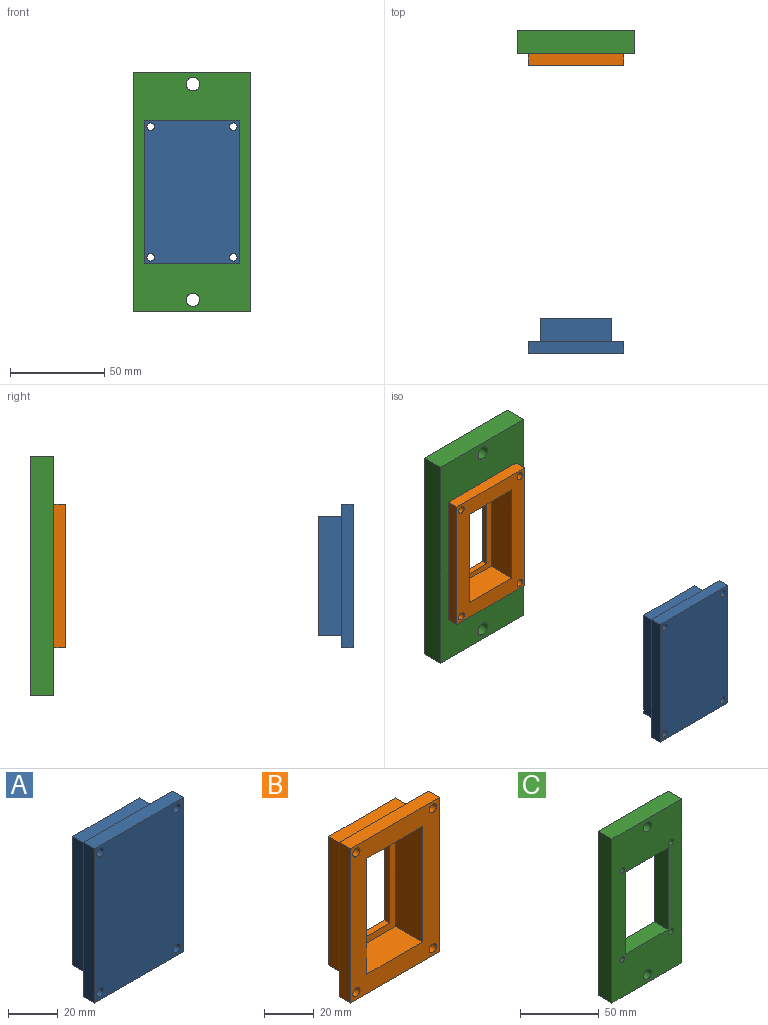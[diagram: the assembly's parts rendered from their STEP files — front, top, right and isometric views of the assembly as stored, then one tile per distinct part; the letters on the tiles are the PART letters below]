
ASSEMBLY  parts=3 mates=4
PART A: 15 faces, bbox 50.8x18.5x76.2 mm
  f0: plane 63.5x12.19mm, normal (1,0,0), area 774.2mm2, adj f1,f3,f4,f10
  f1: plane 38.1x12.19mm, normal (0,0,1), area 464.5mm2, adj f0,f2,f4,f10
  f2: plane 63.5x12.19mm, normal (-1,0,0), area 774.2mm2, adj f1,f3,f4,f10
  f3: plane 38.1x12.19mm, normal (0,0,-1), area 464.5mm2, adj f0,f2,f4,f10
  f4: plane 63.5x38.1mm, normal (0,1,0), area 2419.3mm2, adj f0,f1,f2,f3
  f5: plane 76.2x6.35mm, normal (1,0,0), area 483.9mm2, adj f6,f8,f9,f10
  f6: plane 50.8x6.35mm, normal (0,0,1), area 322.6mm2, adj f5,f7,f9,f10
  f7: plane 76.2x6.35mm, normal (-1,0,0), area 483.9mm2, adj f6,f8,f9,f10
  f8: plane 50.8x6.35mm, normal (0,0,-1), area 322.6mm2, adj f5,f7,f9,f10
  f9: plane 76.2x50.8mm, normal (0,-1,0), area 3817.4mm2, adj f5,f6,f7,f8,f11,f12,f13,f14
  f10: plane 76.2x50.8mm, normal (0,1,0), area 1398.1mm2, adj f0,f1,f2,f3,f5,f6,f7,f8
  f11: cylinder r=2.06mm len=6.35mm, axis (0,1,0), area 82.3mm2, adj f9,f10
  f12: cylinder r=2.06mm len=6.35mm, axis (0,1,0), area 82.3mm2, adj f9,f10
  f13: cylinder r=2.06mm len=6.35mm, axis (0,1,0), area 82.3mm2, adj f9,f10
  f14: cylinder r=2.06mm len=6.35mm, axis (0,1,0), area 82.3mm2, adj f9,f10
PART B: 24 faces, bbox 50.8x18.5x76.2 mm
  f0: plane 76.2x50.8mm, normal (0,-1,0), area 2002.9mm2, adj f10,f11,f12,f13,f15,f16,f17,f18
  f1: plane 50.8x3.05mm, normal (-1,0,0), area 154.8mm2, adj f2,f4,f5,f23
  f2: plane 25.4x3.05mm, normal (0,0,-1), area 77.4mm2, adj f1,f3,f5,f23
  f3: plane 50.8x3.05mm, normal (1,0,0), area 154.8mm2, adj f2,f4,f5,f23
  f4: plane 25.4x3.05mm, normal (0,0,1), area 77.4mm2, adj f1,f3,f5,f23
  f5: plane 63.5x38.1mm, normal (0,1,0), area 1129mm2, adj f1,f2,f3,f4,f6,f7,f8,f9
  f6: plane 63.5x12.19mm, normal (1,0,0), area 774.2mm2, adj f5,f7,f9,f14
  f7: plane 38.1x12.19mm, normal (0,0,1), area 464.5mm2, adj f5,f6,f8,f14
  f8: plane 63.5x12.19mm, normal (-1,0,0), area 774.2mm2, adj f5,f7,f9,f14
  f9: plane 38.1x12.19mm, normal (0,0,-1), area 464.5mm2, adj f5,f6,f8,f14
  f10: plane 76.2x6.35mm, normal (1,0,0), area 483.9mm2, adj f0,f11,f13,f14
  f11: plane 50.8x6.35mm, normal (0,0,1), area 322.6mm2, adj f0,f10,f12,f14
  f12: plane 76.2x6.35mm, normal (-1,0,0), area 483.9mm2, adj f0,f11,f13,f14
  f13: plane 50.8x6.35mm, normal (0,0,-1), area 322.6mm2, adj f0,f10,f12,f14
  f14: plane 76.2x50.8mm, normal (0,1,0), area 1398.1mm2, adj f6,f7,f8,f9,f10,f11,f12,f13
  f15: cylinder r=2.06mm len=6.35mm, axis (0,1,0), area 82.3mm2, adj f0,f14
  f16: cylinder r=2.06mm len=6.35mm, axis (0,1,0), area 82.3mm2, adj f0,f14
  f17: cylinder r=2.06mm len=6.35mm, axis (0,1,0), area 82.3mm2, adj f0,f14
  f18: cylinder r=2.06mm len=6.35mm, axis (0,1,0), area 82.3mm2, adj f0,f14
  f19: plane 57.15x15.49mm, normal (-1,0,0), area 885.5mm2, adj f0,f20,f22,f23
  f20: plane 31.75x15.49mm, normal (0,0,-1), area 491.9mm2, adj f0,f19,f21,f23
  f21: plane 57.15x15.49mm, normal (1,0,0), area 885.5mm2, adj f0,f20,f22,f23
  f22: plane 31.75x15.49mm, normal (0,0,1), area 491.9mm2, adj f0,f19,f21,f23
  f23: plane 57.15x31.75mm, normal (0,-1,0), area 524.2mm2, adj f1,f2,f3,f4,f19,f20,f21,f22
PART C: 16 faces, bbox 62.5x12.2x127 mm
  f0: plane 127x62.48mm, normal (0,-1,0), area 5383.1mm2, adj f2,f3,f4,f5,f6,f7,f8,f9
  f1: plane 127x62.48mm, normal (0,1,0), area 5383.1mm2, adj f2,f3,f4,f5,f6,f7,f8,f9
  f2: plane 127x12.19mm, normal (1,0,0), area 1548.4mm2, adj f0,f1,f3,f5
  f3: plane 62.48x12.19mm, normal (0,0,1), area 761.8mm2, adj f0,f1,f2,f4
  f4: plane 127x12.19mm, normal (-1,0,0), area 1548.4mm2, adj f0,f1,f3,f5
  f5: plane 62.48x12.19mm, normal (0,0,-1), area 761.8mm2, adj f0,f1,f2,f4
  f6: cylinder r=3.56mm len=12.19mm, axis (0,-1,0), area 272.4mm2, adj f0,f1
  f7: cylinder r=3.56mm len=12.19mm, axis (0,-1,0), area 272.4mm2, adj f0,f1
  f8: cylinder r=2.06mm len=12.19mm, axis (0,-1,0), area 158.1mm2, adj f0,f1
  f9: cylinder r=2.06mm len=12.19mm, axis (0,-1,0), area 158.1mm2, adj f0,f1
  f10: cylinder r=2.06mm len=12.19mm, axis (0,-1,0), area 158.1mm2, adj f0,f1
  f11: cylinder r=2.06mm len=12.19mm, axis (0,-1,0), area 158.1mm2, adj f0,f1
  f12: plane 63.5x12.19mm, normal (-1,0,0), area 774.2mm2, adj f0,f1,f13,f15
  f13: plane 38.1x12.19mm, normal (0,0,-1), area 464.5mm2, adj f0,f1,f12,f14
  f14: plane 63.5x12.19mm, normal (1,0,0), area 774.2mm2, adj f0,f1,f13,f15
  f15: plane 38.1x12.19mm, normal (0,0,1), area 464.5mm2, adj f0,f1,f12,f14
PLACE A t=(-4.66,-265.59,-27.56)mm
PLACE B t=(-4.66,-113.28,-27.56)mm
PLACE C t=(-4.66,-113.28,-27.56)mm fixed
MATE planar C.f14 <-> B.f8  axis (1,0,0) through (-23.71,-119.38,-27.56)mm
MATE planar B.f7 <-> C.f13  axis (0,0,1) through (-4.66,-119.38,4.19)mm
MATE planar C.f14 <-> A.f2  axis (1,0,0) through (-23.71,-119.38,-27.56)mm
MATE planar A.f1 <-> C.f13  axis (0,0,1) through (-4.66,-271.69,4.19)mm
